# Revit family: ISI_IdealStandard_WCSeats_Tempo_ShortProjection
name_source: partatom
category: Plumbing Fixtures
revit_build: Autodesk Revit MEP 2012 (Build: 20110309_2315(x64)
units: mm (PartAtom-declared; Revit-internal decimal feet)

## types (2) — shared parameters
Accessories = www.idealspec.co.uk
AreaUnits = millimeters
AssetType = Fixed
Brand = Ideal Standard
Color = White
ConnectionType = Plumbing
Default Elevation = 1219 mm
DurationUnit = year
ECA = No
ExpectedLife = 15
Finish = White
Help = www.idealspec.co.uk/contact-us.html
IfcExportAs = IfcSanitaryTerminalType
InstallationInstructions = www.idealspec.co.uk/resources.html
LinearUnits = millimeters
ManufacturerURL = www.idealspec.co.uk
NBSDescription = WC seats and covers
NBSReference = 45-35-70/391
Name = WCSeats_Tempo-AllVariants_IdealStandard
NettWeight = 2.70 Kg
NominalDepth = 395 mm
NominalHeight = 40 mm  [stored 0.131234 ft]
NominalLength = 395 mm
NominalWidth = 371 mm
ProductInformation = www.idealspec.co.uk/assets/datasheet/T328701
SeatColor = White
SeatHasCover = Yes
SeatMaterial = Plastic
SeatSKU = ISI_IdealStandard_WC_PlasticWhite_Render
SeatType = RingSeat
Shape = Soft Square
Space = Internal
SpareParts = www.fastpart-spares.co.uk
URL = www.idealspec.co.uk
Uniclass2 = Pr_40_20_93_95
Version = 2
VolumeUnits = Litres
WRAS = No
WarrantyDescription = Manufacturers Warranty
WarrantyDurationParts = 5
WarrantyDurationUnit = year
WaterEfficientProduct = No
zero-valued in all types: CWFU, Cost, HWFU, WFU

## per-type parameters (varying)
| type | BIMObjectName | Features | IfcExportType | Material | Model | ModelNumber | Size |
| T679801 - Tempo Seat and Cover for short projection T3287 bow - standard close | ISI_IdealStandard_WCSeats_Tempo_T6798 | Standard close | WCSEAT | Plastic | T679801 | T679801 | 395 x 370 x 40 mm |
| T679901 - Tempo Seat and Cover for short projection T3287 bowl - slow close | ISI_IdealStandard_WCSeats_Tempo_T6799 | Slow close | TOILETPAN | Vitreous China | T679901 | T679901 | 371 x 395 x 40 mm |

note: [stored X ft] marks values corroborated as IEEE doubles in the binary element streams (Revit-internal decimal feet)

## geometry (parser evidence)
native form markers: Blend x1, Sweep x4
no freeform markers — native parametric forms only
